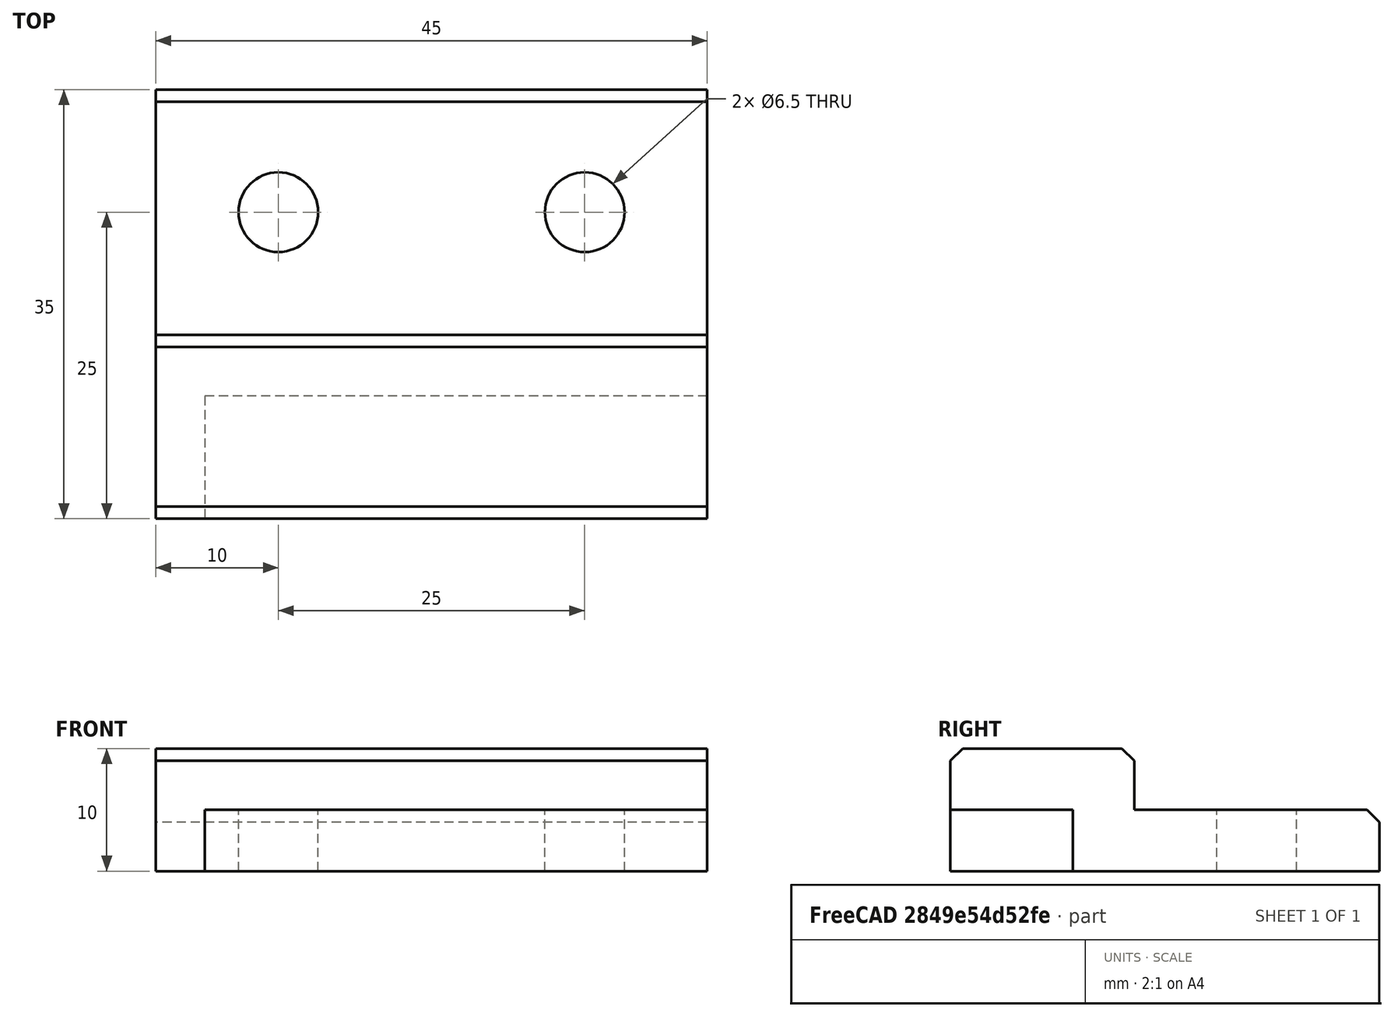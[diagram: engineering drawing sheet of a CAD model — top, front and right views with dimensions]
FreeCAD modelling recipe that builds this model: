
FCSTD DOCUMENT  (FreeCAD 0.14R3703 (Git))
Label: guia_cubeta_pos_der
License: CC-BY 3.0
LicenseURL: http://creativecommons.org/licenses/by/3.0/
objects: Part::Chamfer×4, Part::Box×3, Part::Fuse×2, Part::Cylinder×2, Part::Cut×2, Part::Feature×1
note: 14 computed .brp shape members not serialized (recipe doc carries the construction recipe); baked Part::Feature solids carry a one-line shape summary decoded from their .brp

FEATURE [Part::Box] Box  label="Cubo"
  Height = 5
  Length = 45
  Width = 25
FEATURE [Part::Box] Box001  label="Cubo001"
  Height = 5
  Length = 45
  Placement = pos=(0,20,5) rot=(0,0,1;0rad)
  Width = 15
FEATURE [Part::Chamfer] Chamfer
  Base = -> Box
  Edges = 1 edges r=1: [Edge10]
FEATURE [Part::Chamfer] Chamfer001
  Base = -> Box001
  Edges = 1 edges r=1: [Edge10]
FEATURE [Part::Chamfer] Chamfer002
  Base = -> Chamfer001
  Edges = 1 edges r=1: [Edge13]
FEATURE [Part::Fuse] Fusion
  Base = -> Chamfer
  Tool = -> Chamfer002
FEATURE [Part::Cylinder] Cylinder  label="Cilindro"
  Angle = 360
  Height = 10
  Placement = pos=(10,10,0) rot=(0,0,1;0rad)
  Radius = 3.25
FEATURE [Part::Cut] Cut
  Base = -> Fusion
  Tool = -> Cylinder
FEATURE [Part::Cylinder] Cylinder001  label="Cilindro001"
  Angle = 360
  Height = 10
  Placement = pos=(35,10,0) rot=(0,0,1;0rad)
  Radius = 3.25
FEATURE [Part::Cut] Cut001
  Base = -> Cut
  Tool = -> Cylinder001
FEATURE [Part::Box] Box002  label="Cubo002"
  Height = 10
  Length = 4
  Placement = pos=(0,25,0) rot=(0,0,1;0rad)
  Width = 10
FEATURE [Part::Chamfer] Chamfer003
  Base = -> Box002
  Edges = 1 edges r=1: [Edge12]
  Placement = pos=(41,0,0) rot=(0,0,1;0rad)
FEATURE [Part::Fuse] Fusion001  label="guia_cubeta_pos_der"
  Base = -> Cut001
  Placement = pos=(0,0,0) rot=(0,0,1;3.14159rad)
  Tool = -> Chamfer003
FEATURE [Part::Feature] Fusion001001  label="guia_cubeta_pos_der001"
  Placement = pos=(0,0,0) rot=(0,0,1;3.14159rad)
  shape: bbox 45 x 35 x 10 mm, 16 faces (baked)
